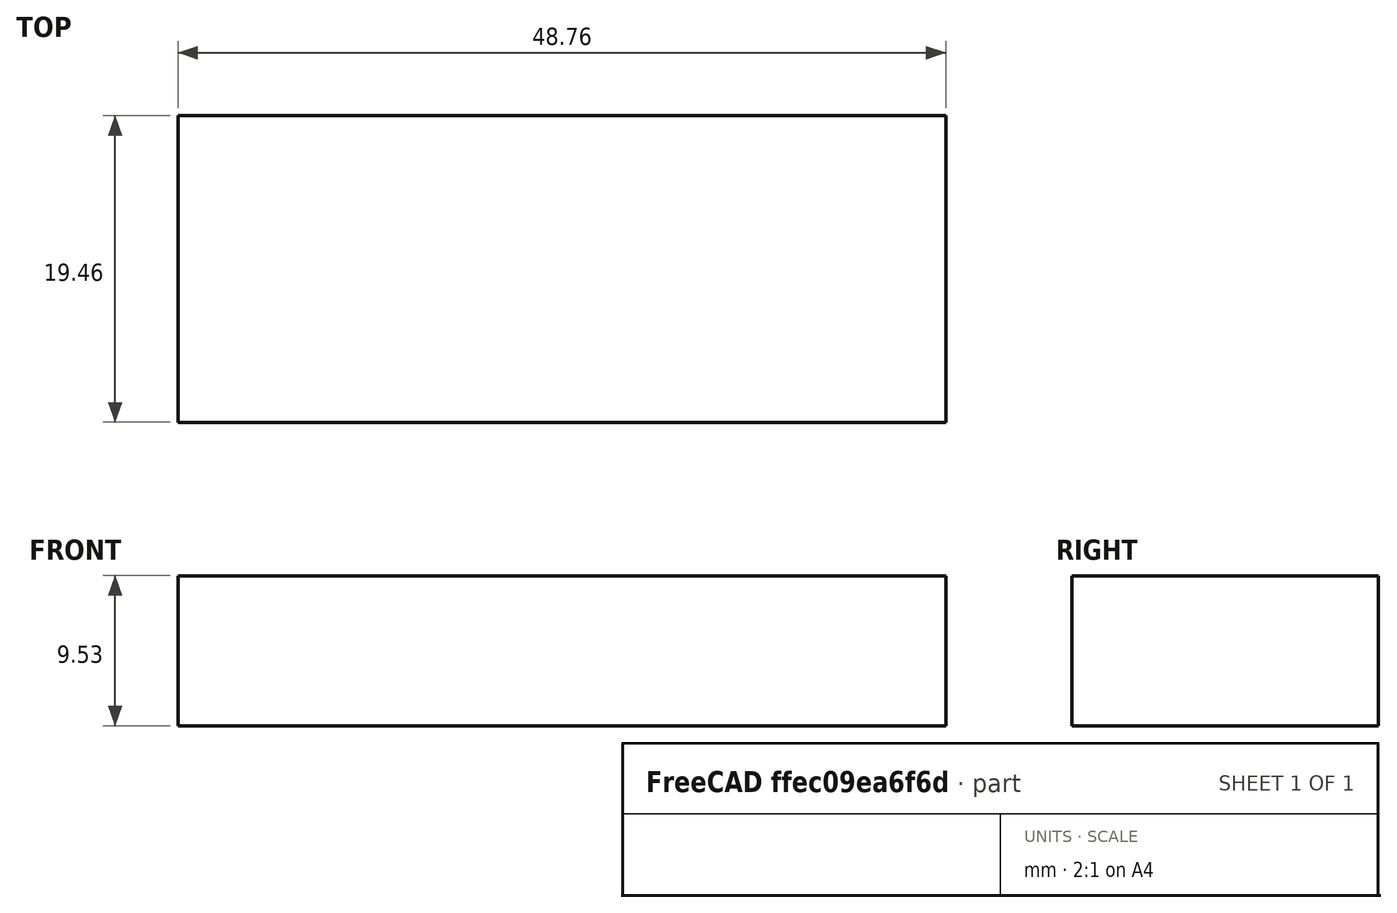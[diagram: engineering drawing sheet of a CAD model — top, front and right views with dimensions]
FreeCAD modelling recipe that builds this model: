
FCSTD DOCUMENT  (FreeCAD 0.15R4671 (Git))
Label: rs
License: All rights reserved
LicenseURL: http://en.wikipedia.org/wiki/All_rights_reserved
objects: Sketcher::SketchObject×1, PartDesign::Pad×1
note: 3 computed .brp shape members not serialized (recipe doc carries the construction recipe); baked Part::Feature solids carry a one-line shape summary decoded from their .brp

FEATURE [Sketcher::SketchObject] Sketch
  sketch-geometry (4):
    g0: LineSegment StartX=-24.384 StartY=9.73455 StartZ=0 EndX=24.384 EndY=9.73455 EndZ=0
    g1: LineSegment StartX=24.384 StartY=9.73455 StartZ=0 EndX=24.384 EndY=-9.73455 EndZ=0
    g2: LineSegment StartX=24.384 StartY=-9.73455 StartZ=0 EndX=-24.384 EndY=-9.73455 EndZ=0
    g3: LineSegment StartX=-24.384 StartY=-9.73455 StartZ=0 EndX=-24.384 EndY=9.73455 EndZ=0
  constraints (11):
    c: Coincident(g0,g1)
    c: Coincident(g1,g2)
    c: Coincident(g2,g3)
    c: Coincident(g3,g0)
    c: Horizontal(g0)
    c: Horizontal(g2)
    c: Vertical(g1)
    c: Vertical(g3)
    c: DistanceY(g1) = -19.4691
    c: DistanceX(g0) = 48.768
    c: Symmetric(g0,g1,g-1)
FEATURE [PartDesign::Pad] Pad
  Length = 9.525
  Length2 = 100
  Sketch = -> Sketch
  Type = 0
